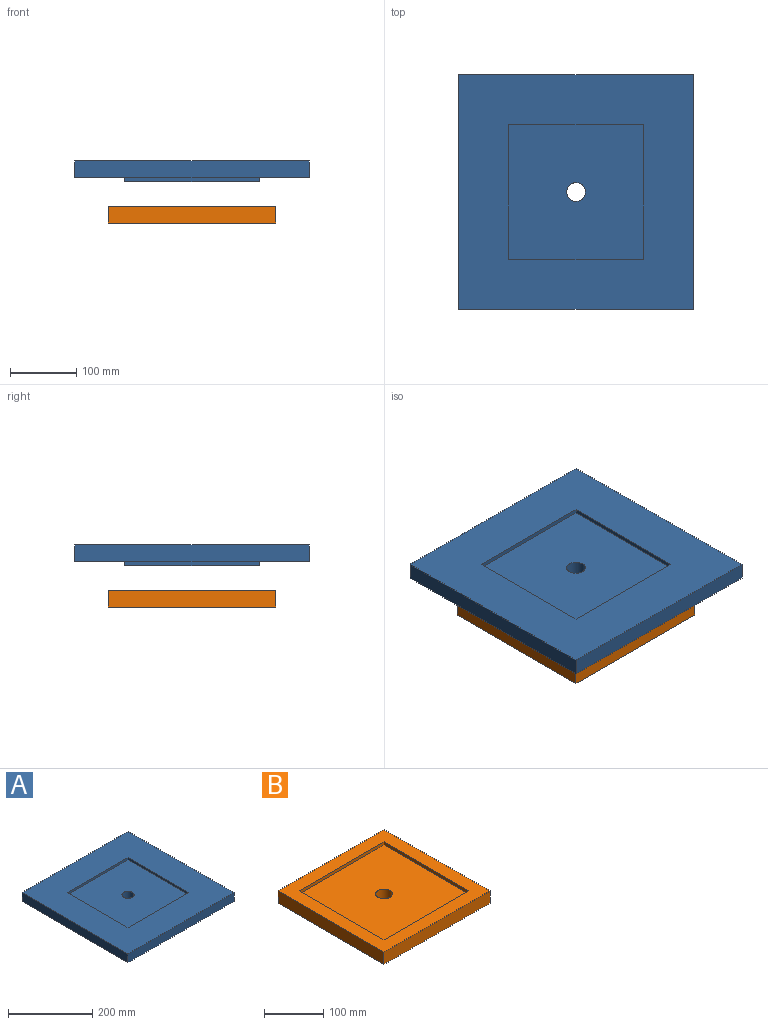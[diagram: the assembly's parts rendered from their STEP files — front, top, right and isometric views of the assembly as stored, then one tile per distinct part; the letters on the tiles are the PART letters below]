
ASSEMBLY  parts=2 mates=1
PART A: 17 faces, bbox 355.6x355.6x31.8 mm
  f0: plane 203.2x6.35mm, normal (1,0,0), area 1290.3mm2, adj f1,f3,f4,f14
  f1: plane 203.2x6.35mm, normal (0,1,0), area 1290.3mm2, adj f0,f2,f4,f14
  f2: plane 203.2x6.35mm, normal (-1,0,0), area 1290.3mm2, adj f1,f3,f4,f14
  f3: plane 203.2x6.35mm, normal (0,-1,0), area 1290.3mm2, adj f0,f2,f4,f14
  f4: plane 203.2x203.2mm, normal (0,0,-1), area 40648.9mm2, adj f0,f1,f2,f3,f16
  f5: plane 203.2x6.35mm, normal (-1,0,0), area 1290.3mm2, adj f6,f8,f13,f15
  f6: plane 203.2x6.35mm, normal (0,-1,0), area 1290.3mm2, adj f5,f7,f13,f15
  f7: plane 203.2x6.35mm, normal (1,0,0), area 1290.3mm2, adj f6,f8,f13,f15
  f8: plane 203.2x6.35mm, normal (0,1,0), area 1290.3mm2, adj f5,f7,f13,f15
  f9: plane 355.6x25.4mm, normal (1,0,0), area 9032.2mm2, adj f10,f12,f13,f14
  f10: plane 355.6x25.4mm, normal (0,1,0), area 9032.2mm2, adj f9,f11,f13,f14
  f11: plane 355.6x25.4mm, normal (-1,0,0), area 9032.2mm2, adj f10,f12,f13,f14
  f12: plane 355.6x25.4mm, normal (0,-1,0), area 9032.2mm2, adj f9,f11,f13,f14
  f13: plane 355.6x355.6mm, normal (0,0,1), area 85161.1mm2, adj f5,f6,f7,f8,f9,f10,f11,f12
  f14: plane 355.6x355.6mm, normal (0,0,-1), area 85161.1mm2, adj f0,f1,f2,f3,f9,f10,f11,f12
  f15: plane 203.2x203.2mm, normal (0,0,1), area 40648.9mm2, adj f5,f6,f7,f8,f16
  f16: cylinder r=14.29mm len=28.58mm, axis (0,0,-1), area 2280.2mm2, adj f4,f15
PART B: 12 faces, bbox 254x254x25.4 mm
  f0: plane 254x25.4mm, normal (0,-1,0), area 6451.6mm2, adj f1,f3,f4,f9
  f1: plane 254x25.4mm, normal (1,0,0), area 6451.6mm2, adj f0,f2,f4,f9
  f2: plane 254x25.4mm, normal (0,1,0), area 6451.6mm2, adj f1,f3,f4,f9
  f3: plane 254x25.4mm, normal (-1,0,0), area 6451.6mm2, adj f0,f2,f4,f9
  f4: plane 254x254mm, normal (0,0,-1), area 63874.7mm2, adj f0,f1,f2,f3,f11
  f5: plane 203.2x6.35mm, normal (-1,0,0), area 1290.3mm2, adj f6,f8,f9,f10
  f6: plane 203.2x6.35mm, normal (0,1,0), area 1290.3mm2, adj f5,f7,f9,f10
  f7: plane 203.2x6.35mm, normal (1,0,0), area 1290.3mm2, adj f6,f8,f9,f10
  f8: plane 203.2x6.35mm, normal (0,-1,0), area 1290.3mm2, adj f5,f7,f9,f10
  f9: plane 254x254mm, normal (0,0,1), area 23225.8mm2, adj f0,f1,f2,f3,f5,f6,f7,f8
  f10: plane 203.2x203.2mm, normal (0,0,1), area 40648.9mm2, adj f5,f6,f7,f8,f11
  f11: cylinder r=14.29mm len=28.58mm, axis (0,0,-1), area 1710.1mm2, adj f4,f10
PLACE A t=(3.08,20.96,-9.79)mm
PLACE B t=(3.08,20.96,-53.03)mm
MATE slider A.f16 <-> B.f11  axis (0,0,-1) through (3.08,20.96,9.26)mm
